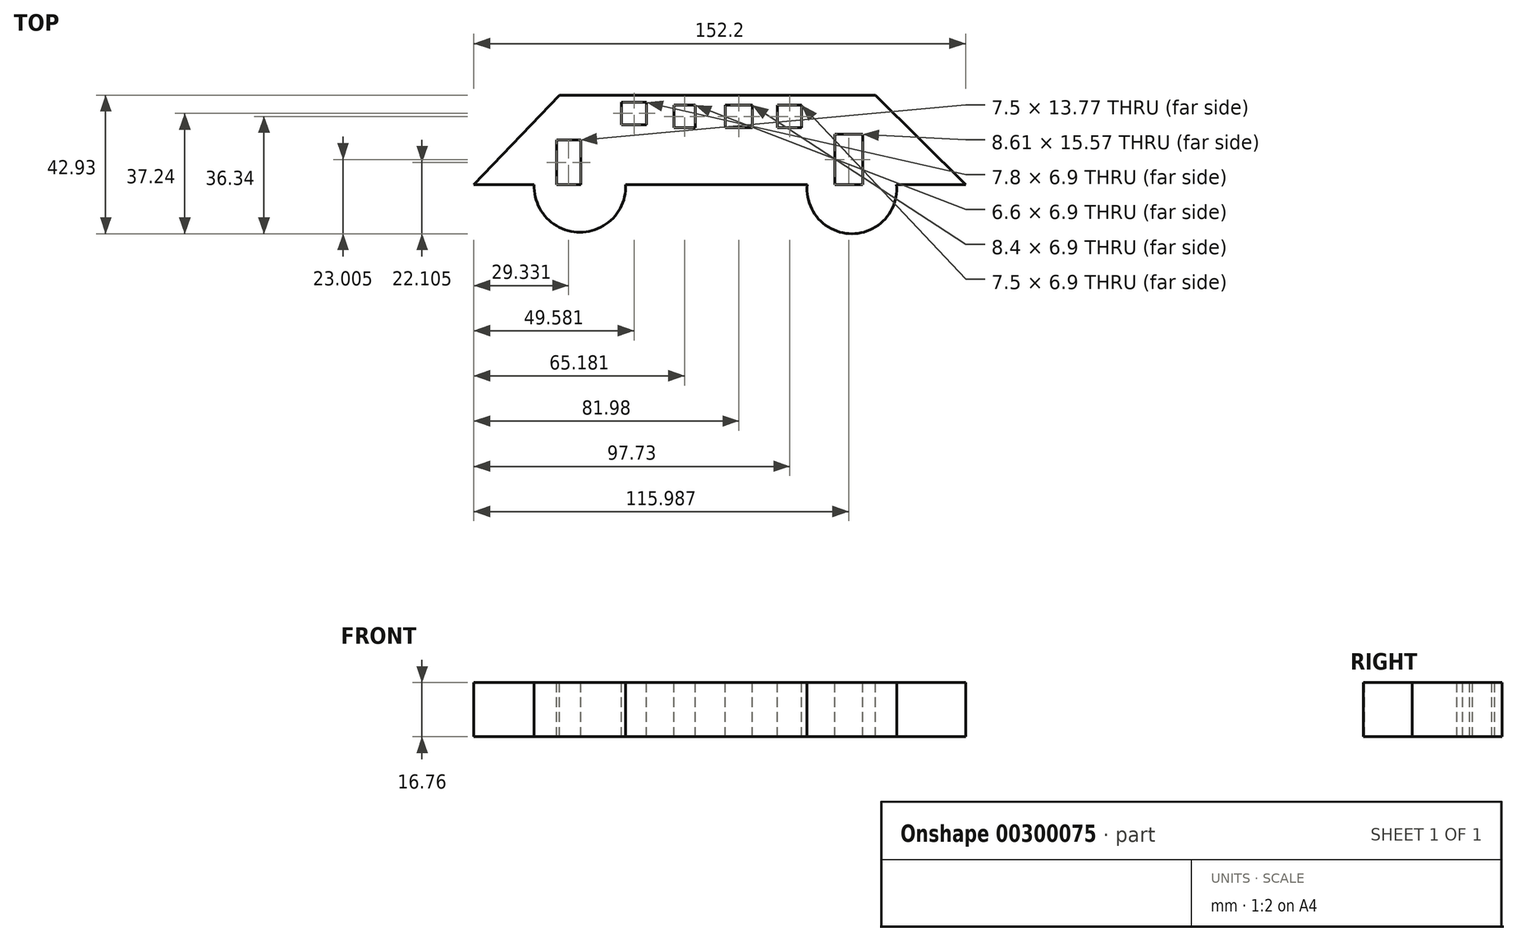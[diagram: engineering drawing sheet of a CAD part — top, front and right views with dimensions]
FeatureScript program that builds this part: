
annotation { "Feature Type Name" : "Feature", "Feature Type Description" : "" }
export const myFeature = defineFeature(function(context is Context, id is Id, definition is map)
    precondition{}
    {
        {
            var Q0;
            Q0=qCreatedBy(makeId("Top.planeOp"),FACE);
            var sketch = newSketch(context, id + "F0", { "sketchPlane" : qUnion([Q0])});
            skLineSegment(sketch, "E0", {"start": v(-75.65, 0) * mm, "end": v(-49.17, 27.7) * mm});
            skLineSegment(sketch, "E1", {"start": v(-49.17, 27.7) * mm, "end": v(48.61, 27.7) * mm});
            skLineSegment(sketch, "E2", {"start": v(48.61, 27.7) * mm, "end": v(76.55, 0) * mm});
            skLineSegment(sketch, "E3", {"start": v(76.55, 0) * mm, "end": v(-75.65, 0) * mm});
            skArc(sketch, "E4", {"start": v(-56.97, 0) * mm, "mid": v(-42.82, -14.76) * mm, "end": v(-28.67, 0) * mm});
            skArc(sketch, "E5", {"start": v(27.54, 0) * mm, "mid": v(41.34, -15.22) * mm, "end": v(55.14, 0) * mm});
            skArc(sketch, "E6", {"start": v(-59.48, 16.92) * mm, "mid": v(-46.1, 18.47) * mm, "end": v(-36.27, 27.7) * mm});
            skArc(sketch, "E7", {"start": v(35.13, 27.7) * mm, "mid": v(44.64, 18.73) * mm, "end": v(57.73, 18.67) * mm});
            skLineSegment(sketch, "E8.bottom", {"start": v(-29.97, 25.47) * mm, "end": v(-22.17, 25.47) * mm});
            skLineSegment(sketch, "E8.top", {"start": v(-29.97, 18.57) * mm, "end": v(-22.17, 18.57) * mm});
            skLineSegment(sketch, "E8.left", {"start": v(-29.97, 25.47) * mm, "end": v(-29.97, 18.57) * mm});
            skLineSegment(sketch, "E8.right", {"start": v(-22.17, 25.47) * mm, "end": v(-22.17, 18.57) * mm});
            skLineSegment(sketch, "E9.bottom", {"start": v(-13.77, 24.57) * mm, "end": v(-7.17, 24.57) * mm});
            skLineSegment(sketch, "E9.top", {"start": v(-13.77, 17.67) * mm, "end": v(-7.17, 17.67) * mm});
            skLineSegment(sketch, "E9.left", {"start": v(-13.77, 24.57) * mm, "end": v(-13.77, 17.67) * mm});
            skLineSegment(sketch, "E9.right", {"start": v(-7.17, 24.57) * mm, "end": v(-7.17, 17.67) * mm});
            skLineSegment(sketch, "E10.bottom", {"start": v(2.13, 24.57) * mm, "end": v(10.53, 24.57) * mm});
            skLineSegment(sketch, "E10.top", {"start": v(2.13, 17.67) * mm, "end": v(10.53, 17.67) * mm});
            skLineSegment(sketch, "E10.left", {"start": v(2.13, 24.57) * mm, "end": v(2.13, 17.67) * mm});
            skLineSegment(sketch, "E10.right", {"start": v(10.53, 24.57) * mm, "end": v(10.53, 17.67) * mm});
            skLineSegment(sketch, "E11.bottom", {"start": v(18.33, 24.57) * mm, "end": v(25.83, 24.57) * mm});
            skLineSegment(sketch, "E11.top", {"start": v(18.33, 17.67) * mm, "end": v(25.83, 17.67) * mm});
            skLineSegment(sketch, "E11.left", {"start": v(18.33, 24.57) * mm, "end": v(18.33, 17.67) * mm});
            skLineSegment(sketch, "E11.right", {"start": v(25.83, 24.57) * mm, "end": v(25.83, 17.67) * mm});
            skLineSegment(sketch, "E12.bottom", {"start": v(-50.07, 0) * mm, "end": v(-42.57, 0) * mm});
            skLineSegment(sketch, "E12.top", {"start": v(-50.07, 13.77) * mm, "end": v(-42.57, 13.77) * mm});
            skLineSegment(sketch, "E12.left", {"start": v(-50.07, 0) * mm, "end": v(-50.07, 13.77) * mm});
            skLineSegment(sketch, "E12.right", {"start": v(-42.57, 0) * mm, "end": v(-42.57, 13.77) * mm});
            skPoint(sketch, "E13.oppositeSnap0", {"position": v(44.64, 18.73) * mm});
            skLineSegment(sketch, "E13.bottom", {"start": v(36.03, 0) * mm, "end": v(44.64, 0) * mm});
            skLineSegment(sketch, "E13.top", {"start": v(36.03, 15.57) * mm, "end": v(44.64, 15.57) * mm});
            skLineSegment(sketch, "E13.left", {"start": v(36.03, 0) * mm, "end": v(36.03, 15.57) * mm});
            skLineSegment(sketch, "E13.right", {"start": v(44.64, 0) * mm, "end": v(44.64, 15.57) * mm});
            skLineSegment(sketch, "E14.bottom", {"start": v(-30.27, 13.47) * mm, "end": v(-14.37, 13.47) * mm});
            skLineSegment(sketch, "E14.top", {"start": v(-30.27, 0) * mm, "end": v(-14.37, 0) * mm});
            skLineSegment(sketch, "E14.left", {"start": v(-30.27, 13.47) * mm, "end": v(-30.27, 0) * mm});
            skLineSegment(sketch, "E14.right", {"start": v(-14.37, 13.47) * mm, "end": v(-14.37, 0) * mm});
            skLineSegment(sketch, "E15.bottom", {"start": v(-14.37, 13.47) * mm, "end": v(3.03, 13.47) * mm});
            skLineSegment(sketch, "E15.top", {"start": v(-14.37, 0) * mm, "end": v(3.03, 0) * mm});
            skLineSegment(sketch, "E15.right", {"start": v(3.03, 13.47) * mm, "end": v(3.03, 0) * mm});
            skLineSegment(sketch, "E16.bottom", {"start": v(3.03, 13.47) * mm, "end": v(22.83, 13.47) * mm});
            skLineSegment(sketch, "E16.top", {"start": v(3.03, 0) * mm, "end": v(22.83, 0) * mm});
            skLineSegment(sketch, "E16.right", {"start": v(22.83, 13.47) * mm, "end": v(22.83, 0) * mm});
            skSolve(sketch);
        }
        {
            var Q0;
            {var subQ1=sQuery(id+"F0.wireOp",EDGE,"E6");Q0=makeQuery(id+"F0.imprint","IMPRINT",FACE,{"disambiguationData":[TD([[makeQuery(id+"F0.imprint","IMPRINT",EDGE,{"derivedFrom":subQ1}),-1.0]])]});}
            var Q1;
            {var subQ3=sQuery(id+"F0.wireOp",EDGE,"E6");Q1=makeQuery(id+"F0.imprint","IMPRINT",FACE,{"disambiguationData":[TD([[makeQuery(id+"F0.imprint","IMPRINT",EDGE,{"derivedFrom":subQ3}),1.0]])]});}
            var Q2;
            {var subQ3=sQuery(id+"F0.wireOp",EDGE,"E7");Q2=makeQuery(id+"F0.imprint","IMPRINT",FACE,{"disambiguationData":[TD([[makeQuery(id+"F0.imprint","IMPRINT",EDGE,{"derivedFrom":subQ3}),1.0]])]});}
            var Q3;
            Q3=makeQuery(id+"F0.imprint","IMPRINT",FACE,{"disambiguationData":[TD([[makeQuery(id+"F0.imprint","IMPRINT",EDGE,{"derivedFrom":sQuery(id+"F0.wireOp",EDGE,"E15.bottom")}),-1.0]])]});
            var Q4;
            Q4=makeQuery(id+"F0.imprint","IMPRINT",FACE,{"disambiguationData":[TD([[makeQuery(id+"F0.imprint","IMPRINT",EDGE,{"derivedFrom":sQuery(id+"F0.wireOp",EDGE,"E16.bottom")}),-1.0]])]});
            var Q5;
            Q5=makeQuery(id+"F0.imprint","IMPRINT",FACE,{"disambiguationData":[TD([[makeQuery(id+"F0.imprint","IMPRINT",EDGE,{"derivedFrom":sQuery(id+"F0.wireOp",EDGE,"E14.bottom")}),-1.0]])]});
            var Q6;
            {var subQ0=sQuery(id+"F0.wireOp",EDGE,"E5");Q6=makeQuery(id+"F0.imprint","IMPRINT",FACE,{"disambiguationData":[TD([[makeQuery(id+"F0.imprint","IMPRINT",EDGE,{"derivedFrom":subQ0}),1.0]])]});}
            var Q7;
            {var subQ1=sQuery(id+"F0.wireOp",EDGE,"E4");Q7=makeQuery(id+"F0.imprint","IMPRINT",FACE,{"disambiguationData":[TD([[makeQuery(id+"F0.imprint","IMPRINT",EDGE,{"derivedFrom":subQ1}),1.0]])]});}
            extrude(context, id + "F1", {"entities" : qUnion([Q0, Q1, Q2, Q3, Q4, Q5, Q6, Q7]), "oppositeDirection" : true, "depth" : 16.76 * mm});
        }
    });
